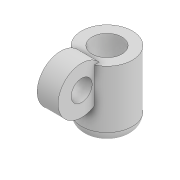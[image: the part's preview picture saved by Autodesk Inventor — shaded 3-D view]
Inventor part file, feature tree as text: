
AUTODESK INVENTOR PART (.ipt)
format: ipt  version: 2022 (Build 260153000, 153)  size: 131,584 bytes
history: native  units: mm
features: extrude x4, sketch x3, projected_geometry x2, fillet x1
ambient origin geometry x8: Origin, YZ Plane, XZ Plane, XY Plane, X Axis, Y Axis, Z Axis, Center Point
bodies: Solid1 (feature_tree)
feature tree (10):
  sketch  "Sketch1"  dims[d0=5.7mm d1=2.0mm]
  extrude  "Extrusion1"  Depth=2.0mm
  extrude  "Extrusion2"  Depth=10.0mm
  extrude  "Extrusion3"  Depth=2.0mm
  fillet  "Fillet1"  Radius=4.0mm
  extrude  "Extrusion4"  Depth=3.0mm TaperAngle=0.0deg
  sketch  "Sketch2"  dims[d2=10.0mm d3=0.0mm d4=4.0mm]
  projected_geometry  "Projected Loop1"
  sketch  "Sketch3"  dims[d5=9.0mm d6=7.0mm d7=4.0mm d8=0.0mm d9=3.0mm d10=0.0mm d11=2.0mm d12=100.0mm d13=0.0mm]
  projected_geometry  "Projected Loop2"
